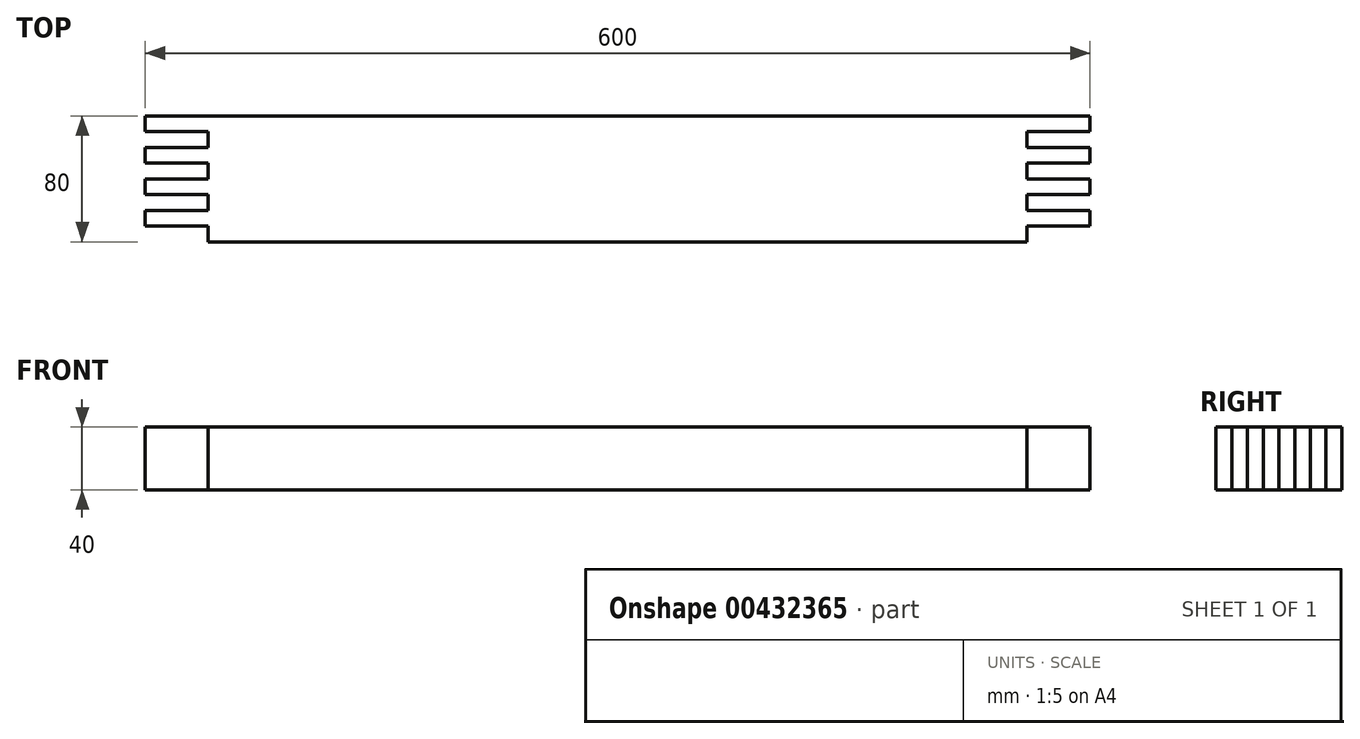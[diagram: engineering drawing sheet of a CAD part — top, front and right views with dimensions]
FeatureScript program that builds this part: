
annotation { "Feature Type Name" : "Feature", "Feature Type Description" : "" }
export const myFeature = defineFeature(function(context is Context, id is Id, definition is map)
    precondition{}
    {
        {
            var Q0;
            Q0=qCreatedBy(makeId("Top.planeOp"),FACE);
            var sketch = newSketch(context, id + "F0", { "sketchPlane" : qUnion([Q0])});
            skLineSegment(sketch, "E0.bottom", {"start": v(-260, -40) * mm, "end": v(260, -40) * mm});
            skPoint(sketch, "E0.middle", {"position": v(0, 0) * mm});
            skLineSegment(sketch, "E1", {"start": v(-260, -40) * mm, "end": v(-260, -30) * mm});
            skLineSegment(sketch, "E2", {"start": v(-260, -30) * mm, "end": v(-300, -30) * mm});
            skLineSegment(sketch, "E3", {"start": v(-300, -30) * mm, "end": v(-300, -20) * mm});
            skLineSegment(sketch, "E4", {"start": v(-300, -20) * mm, "end": v(-260, -20) * mm});
            skLineSegment(sketch, "E5", {"start": v(-260, -20) * mm, "end": v(-260, -10) * mm});
            skLineSegment(sketch, "E6", {"start": v(-260, -10) * mm, "end": v(-300, -10) * mm});
            skLineSegment(sketch, "E7", {"start": v(-300, -10) * mm, "end": v(-300, 0) * mm});
            skLineSegment(sketch, "E8", {"start": v(-300, 0) * mm, "end": v(-260, 0) * mm});
            skLineSegment(sketch, "E9", {"start": v(-260, 0) * mm, "end": v(-260, 10) * mm});
            skLineSegment(sketch, "E10", {"start": v(-260, 10) * mm, "end": v(-300, 10) * mm});
            skLineSegment(sketch, "E11", {"start": v(-300, 10) * mm, "end": v(-300, 20) * mm});
            skLineSegment(sketch, "E12", {"start": v(-300, 20) * mm, "end": v(-260, 20) * mm});
            skLineSegment(sketch, "E13", {"start": v(-260, 20) * mm, "end": v(-260, 30) * mm});
            skLineSegment(sketch, "E14", {"start": v(-260, 30) * mm, "end": v(-300, 30) * mm});
            skLineSegment(sketch, "E15", {"start": v(-300, 30) * mm, "end": v(-300, 40) * mm});
            skLineSegment(sketch, "E16", {"start": v(300, 40) * mm, "end": v(300, 30) * mm});
            skLineSegment(sketch, "E17", {"start": v(300, 30) * mm, "end": v(260, 30) * mm});
            skLineSegment(sketch, "E18", {"start": v(260, 30) * mm, "end": v(260, 20) * mm});
            skLineSegment(sketch, "E19", {"start": v(260, 20) * mm, "end": v(300, 20) * mm});
            skLineSegment(sketch, "E20", {"start": v(300, 20) * mm, "end": v(300, 10) * mm});
            skLineSegment(sketch, "E21", {"start": v(300, 10) * mm, "end": v(260, 10) * mm});
            skLineSegment(sketch, "E22", {"start": v(260, 10) * mm, "end": v(260, 0) * mm});
            skLineSegment(sketch, "E23", {"start": v(260, 0) * mm, "end": v(300, 0) * mm});
            skLineSegment(sketch, "E24", {"start": v(300, 0) * mm, "end": v(300, -10) * mm});
            skLineSegment(sketch, "E25", {"start": v(300, -10) * mm, "end": v(260, -10) * mm});
            skLineSegment(sketch, "E26", {"start": v(260, -10) * mm, "end": v(260, -20) * mm});
            skLineSegment(sketch, "E27", {"start": v(260, -20) * mm, "end": v(300, -20) * mm});
            skLineSegment(sketch, "E28", {"start": v(300, -20) * mm, "end": v(300, -30) * mm});
            skLineSegment(sketch, "E29", {"start": v(300, -30) * mm, "end": v(260, -30) * mm});
            skLineSegment(sketch, "E30", {"start": v(260, -30) * mm, "end": v(260, -40) * mm});
            skLineSegment(sketch, "E31", {"start": v(-300, 40) * mm, "end": v(300, 40) * mm});
            skSolve(sketch);
        }
        {
            var Q0;
            Q0=makeQuery(id+"F0.imprint","IMPRINT",FACE,{"disambiguationData":[TD([[makeQuery(id+"F0.imprint","IMPRINT",EDGE,{"derivedFrom":sQuery(id+"F0.wireOp",EDGE,"E0.bottom")}),1.0]])]});
            extrude(context, id + "F1", {"entities" : qUnion([Q0]), "endBound" : BoundingType.SYMMETRIC, "depth" : 40 * mm});
        }
    });
